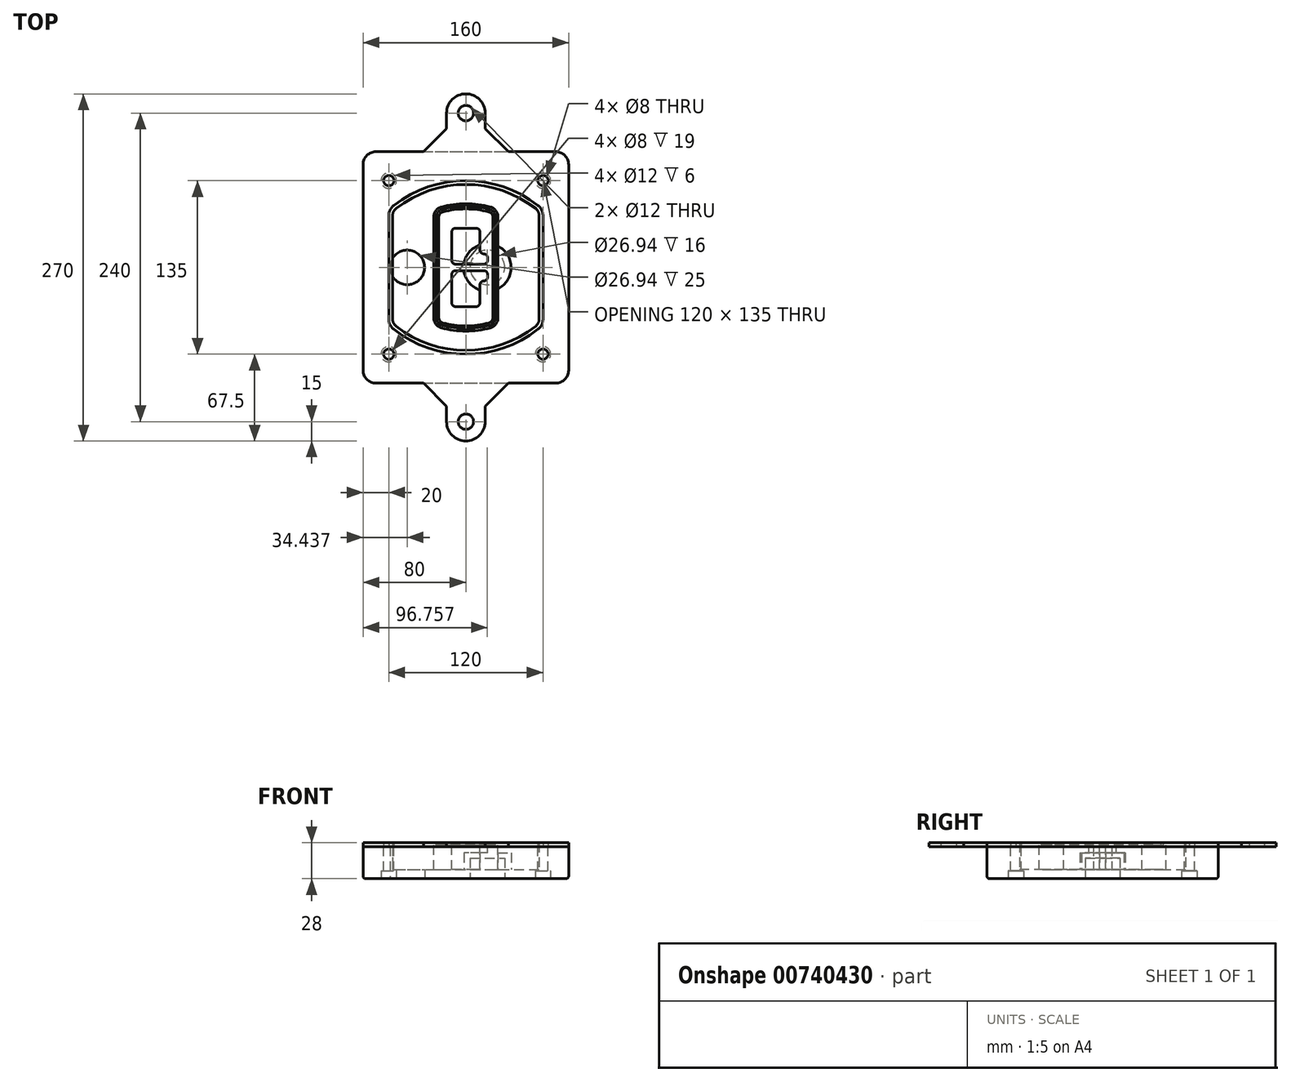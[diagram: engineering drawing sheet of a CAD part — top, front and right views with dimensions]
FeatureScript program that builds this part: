
annotation { "Feature Type Name" : "Feature", "Feature Type Description" : "" }
export const myFeature = defineFeature(function(context is Context, id is Id, definition is map)
    precondition{}
    {
        {
            var Q0;
            Q0=qCreatedBy(makeId("Top.planeOp"),FACE);
            var sketch = newSketch(context, id + "F0", { "sketchPlane" : qUnion([Q0])});
            skPoint(sketch, "E0.rect.middle", {"position": v(0, 0) * mm});
            skLineSegment(sketch, "E1.bottom", {"start": v(-70, -90) * mm, "end": v(70, -90) * mm});
            skLineSegment(sketch, "E1.top", {"start": v(-70, 90) * mm, "end": v(70, 90) * mm});
            skLineSegment(sketch, "E1.left", {"start": v(-80, -80) * mm, "end": v(-80, 80) * mm});
            skLineSegment(sketch, "E1.right", {"start": v(80, -80) * mm, "end": v(80, 80) * mm});
            skLineSegment(sketch, "E2", {"start": v(-80, 90) * mm, "end": v(80, -90) * mm, "construction": true});
            skLineSegment(sketch, "E3", {"start": v(80, 90) * mm, "end": v(-80, -90) * mm, "construction": true});
            skCircle(sketch, "E4", {"center": v(-60, 67.5) * mm, "radius": 4 * mm});
            skCircle(sketch, "E5", {"center": v(60, 67.5) * mm, "radius": 4 * mm});
            skCircle(sketch, "E6", {"center": v(60, -67.5) * mm, "radius": 4 * mm});
            skCircle(sketch, "E7", {"center": v(-60, -67.5) * mm, "radius": 4 * mm});
            skLineSegment(sketch, "E8", {"start": v(-60, 67.5) * mm, "end": v(60, 67.5) * mm, "construction": true});
            skLineSegment(sketch, "E9", {"start": v(60, 67.5) * mm, "end": v(60, -67.5) * mm, "construction": true});
            skLineSegment(sketch, "E10", {"start": v(60, -67.5) * mm, "end": v(-60, -67.5) * mm, "construction": true});
            skLineSegment(sketch, "E11", {"start": v(-60, -67.5) * mm, "end": v(-60, 67.5) * mm, "construction": true});
            skLineSegment(sketch, "E12", {"start": v(-60, 40.3) * mm, "end": v(-60, -40.3) * mm});
            skLineSegment(sketch, "E13", {"start": v(60, 40.3) * mm, "end": v(60, -40.3) * mm});
            skArc(sketch, "E14", {"start": v(56.15, 48.18) * mm, "mid": v(0, 67.5) * mm, "end": v(-56.15, 48.18) * mm});
            skArc(sketch, "E15", {"start": v(-56.15, -48.18) * mm, "mid": v(0, -67.5) * mm, "end": v(56.15, -48.18) * mm});
            skLineSegment(sketch, "E16", {"start": v(-60, 0) * mm, "end": v(60, 0) * mm, "construction": true});
            skPoint(sketch, "E17.visualSharp", {"position": v(-60, -45) * mm});
            skArc(sketch, "E17.filletArc", {"start": v(-60, -40.3) * mm, "mid": v(-58.99, -44.68) * mm, "end": v(-56.15, -48.18) * mm});
            skPoint(sketch, "E18.visualSharp", {"position": v(-60, 45) * mm});
            skArc(sketch, "E18.filletArc", {"start": v(-56.15, 48.18) * mm, "mid": v(-58.99, 44.68) * mm, "end": v(-60, 40.3) * mm});
            skPoint(sketch, "E19.visualSharp", {"position": v(60, 45) * mm});
            skArc(sketch, "E19.filletArc", {"start": v(60, 40.3) * mm, "mid": v(58.99, 44.68) * mm, "end": v(56.15, 48.18) * mm});
            skPoint(sketch, "E20.visualSharp", {"position": v(60, -45) * mm});
            skArc(sketch, "E20.filletArc", {"start": v(56.15, -48.18) * mm, "mid": v(58.99, -44.68) * mm, "end": v(60, -40.3) * mm});
            skPoint(sketch, "E21.visualSharp", {"position": v(-80, 90) * mm});
            skArc(sketch, "E21.filletArc", {"start": v(-70, 90) * mm, "mid": v(-77.07, 87.07) * mm, "end": v(-80, 80) * mm});
            skPoint(sketch, "E22.visualSharp", {"position": v(80, 90) * mm});
            skArc(sketch, "E22.filletArc", {"start": v(80, 80) * mm, "mid": v(77.07, 87.07) * mm, "end": v(70, 90) * mm});
            skPoint(sketch, "E23.visualSharp", {"position": v(80, -90) * mm});
            skArc(sketch, "E23.filletArc", {"start": v(70, -90) * mm, "mid": v(77.07, -87.07) * mm, "end": v(80, -80) * mm});
            skPoint(sketch, "E24.visualSharp", {"position": v(-80, -90) * mm});
            skArc(sketch, "E24.filletArc", {"start": v(-80, -80) * mm, "mid": v(-77.07, -87.07) * mm, "end": v(-70, -90) * mm});
            skArc(sketch, "E25.0", {"start": v(57, 40.3) * mm, "mid": v(56.3, 43.36) * mm, "end": v(54.3, 45.81) * mm});
            skLineSegment(sketch, "E25.1", {"start": v(57, 40.3) * mm, "end": v(57, -40.3) * mm});
            skArc(sketch, "E25.2", {"start": v(54.3, -45.81) * mm, "mid": v(56.3, -43.36) * mm, "end": v(57, -40.3) * mm});
            skArc(sketch, "E25.3", {"start": v(-54.3, -45.81) * mm, "mid": v(0, -64.5) * mm, "end": v(54.3, -45.81) * mm});
            skArc(sketch, "E25.4", {"start": v(-57, -40.3) * mm, "mid": v(-56.3, -43.36) * mm, "end": v(-54.3, -45.81) * mm});
            skArc(sketch, "E25.5", {"start": v(54.3, 45.81) * mm, "mid": v(0, 64.5) * mm, "end": v(-54.3, 45.81) * mm});
            skLineSegment(sketch, "E25.6", {"start": v(-57, 40.3) * mm, "end": v(-57, -40.3) * mm});
            skArc(sketch, "E25.7", {"start": v(-54.3, 45.81) * mm, "mid": v(-56.3, 43.36) * mm, "end": v(-57, 40.3) * mm});
            skArc(sketch, "E26.0", {"start": v(-58.62, 51.33) * mm, "mid": v(-62.58, 46.43) * mm, "end": v(-64, 40.3) * mm});
            skArc(sketch, "E26.1", {"start": v(58.62, 51.33) * mm, "mid": v(0, 71.5) * mm, "end": v(-58.62, 51.33) * mm});
            skArc(sketch, "E26.2", {"start": v(64, 40.3) * mm, "mid": v(62.58, 46.43) * mm, "end": v(58.62, 51.33) * mm});
            skLineSegment(sketch, "E26.3", {"start": v(64, 40.3) * mm, "end": v(64, -40.3) * mm});
            skArc(sketch, "E26.4", {"start": v(58.62, -51.33) * mm, "mid": v(62.58, -46.43) * mm, "end": v(64, -40.3) * mm});
            skLineSegment(sketch, "E26.5", {"start": v(-64, 40.3) * mm, "end": v(-64, -40.3) * mm});
            skArc(sketch, "E26.6", {"start": v(-58.62, -51.33) * mm, "mid": v(0, -71.5) * mm, "end": v(58.62, -51.33) * mm});
            skArc(sketch, "E26.7", {"start": v(-64, -40.3) * mm, "mid": v(-62.58, -46.43) * mm, "end": v(-58.62, -51.33) * mm});
            skSolve(sketch);
        }
        {
            var Q0;
            Q0=makeQuery(id+"F0.imprint","IMPRINT",FACE,{"disambiguationData":[TD([[makeQuery(id+"F0.imprint","IMPRINT",EDGE,{"derivedFrom":sQuery(id+"F0.wireOp",EDGE,"E1.bottom")}),1.0]])]});
            var Q1;
            Q1=makeQuery(id+"F0.imprint","IMPRINT",FACE,{"disambiguationData":[TD([[makeQuery(id+"F0.imprint","IMPRINT",EDGE,{"derivedFrom":sQuery(id+"F0.wireOp",EDGE,"E12")}),1.0]])]});
            var Q2;
            Q2=makeQuery(id+"F0.imprint","IMPRINT",FACE,{"disambiguationData":[TD([[makeQuery(id+"F0.imprint","IMPRINT",EDGE,{"derivedFrom":sQuery(id+"F0.wireOp",EDGE,"E25.0")}),1.0]])]});
            var Q3;
            Q3=makeQuery(id+"F0.imprint","IMPRINT",FACE,{"disambiguationData":[TD([[makeQuery(id+"F0.imprint","IMPRINT",EDGE,{"derivedFrom":sQuery(id+"F0.wireOp",EDGE,"E12")}),-1.0]])]});
            extrude(context, id + "F1", {"entities" : qUnion([Q0, Q1, Q2, Q3]), "oppositeDirection" : true, "depth" : 25 * mm});
        }
        {
            var Q0;
            Q0=makeQuery(id+"F0.imprint","IMPRINT",FACE,{"disambiguationData":[TD([[makeQuery(id+"F0.imprint","IMPRINT",EDGE,{"derivedFrom":sQuery(id+"F0.wireOp",EDGE,"E12")}),1.0]])]});
            extrude(context, id + "F2", {"entities" : qUnion([Q0]), "operationType" : NewBodyOperationType.ADD, "depth" : 3 * mm});
        }
        {
            var Q0;
            Q0=makeQuery(id+"F0.imprint","IMPRINT",FACE,{"disambiguationData":[TD([[makeQuery(id+"F0.imprint","IMPRINT",EDGE,{"derivedFrom":sQuery(id+"F0.wireOp",EDGE,"E25.0")}),1.0]])]});
            extrude(context, id + "F3", {"entities" : qUnion([Q0]), "operationType" : NewBodyOperationType.REMOVE, "oppositeDirection" : true, "depth" : 18 * mm});
        }
        {
            var Q0;
            Q0=makeQuery(id+"F2.opExtrude","CAP_FACE",FACE,{"disambiguationData":[OSD([sQuery(id+"F0.wireOp",EDGE,"E12"),sQuery(id+"F0.wireOp",EDGE,"E13"),sQuery(id+"F0.wireOp",EDGE,"E14"),sQuery(id+"F0.wireOp",EDGE,"E15"),sQuery(id+"F0.wireOp",EDGE,"E17.filletArc"),sQuery(id+"F0.wireOp",EDGE,"E18.filletArc"),sQuery(id+"F0.wireOp",EDGE,"E19.filletArc"),sQuery(id+"F0.wireOp",EDGE,"E20.filletArc"),sQuery(id+"F0.wireOp",EDGE,"E25.0"),sQuery(id+"F0.wireOp",EDGE,"E25.1"),sQuery(id+"F0.wireOp",EDGE,"E25.2"),sQuery(id+"F0.wireOp",EDGE,"E25.3"),sQuery(id+"F0.wireOp",EDGE,"E25.4"),sQuery(id+"F0.wireOp",EDGE,"E25.5"),sQuery(id+"F0.wireOp",EDGE,"E25.6"),sQuery(id+"F0.wireOp",EDGE,"E25.7")])],"isStart":false});
            var sketch = newSketch(context, id + "F4", { "sketchPlane" : qUnion([Q0])});
            skArc(sketch, "E27.0", {"start": v(-19.08, -46.97) * mm, "mid": v(0, -49.5) * mm, "end": v(19.08, -46.97) * mm});
            skArc(sketch, "E28.0", {"start": v(19.08, 46.97) * mm, "mid": v(0, 49.5) * mm, "end": v(-19.08, 46.97) * mm});
            skLineSegment(sketch, "E29", {"start": v(-25, 39.25) * mm, "end": v(-25, -39.25) * mm});
            skLineSegment(sketch, "E30", {"start": v(25, 39.25) * mm, "end": v(25, -39.25) * mm});
            skLineSegment(sketch, "E31", {"start": v(-25, 45.1) * mm, "end": v(25, 45.1) * mm, "construction": true});
            skLineSegment(sketch, "E32", {"start": v(-25, -45.1) * mm, "end": v(25, -45.1) * mm, "construction": true});
            skPoint(sketch, "E33.visualSharp", {"position": v(-25, 45.1) * mm});
            skArc(sketch, "E33.filletArc", {"start": v(-19.08, 46.97) * mm, "mid": v(-23.35, 44.11) * mm, "end": v(-25, 39.25) * mm});
            skPoint(sketch, "E34.visualSharp", {"position": v(25, 45.1) * mm});
            skArc(sketch, "E34.filletArc", {"start": v(25, 39.25) * mm, "mid": v(23.35, 44.11) * mm, "end": v(19.08, 46.97) * mm});
            skPoint(sketch, "E35.visualSharp", {"position": v(25, -45.1) * mm});
            skArc(sketch, "E35.filletArc", {"start": v(19.08, -46.97) * mm, "mid": v(23.35, -44.11) * mm, "end": v(25, -39.25) * mm});
            skPoint(sketch, "E36.visualSharp", {"position": v(-25, -45.1) * mm});
            skArc(sketch, "E36.filletArc", {"start": v(-25, -39.25) * mm, "mid": v(-23.35, -44.11) * mm, "end": v(-19.08, -46.97) * mm});
            skArc(sketch, "E37.0", {"start": v(54.3, 45.81) * mm, "mid": v(0, 64.5) * mm, "end": v(-54.3, 45.81) * mm});
            skArc(sketch, "E37.1", {"start": v(-54.3, 45.81) * mm, "mid": v(-56.3, 43.36) * mm, "end": v(-57, 40.3) * mm});
            skLineSegment(sketch, "E37.2", {"start": v(-57, 40.3) * mm, "end": v(-57, -40.3) * mm});
            skArc(sketch, "E37.3", {"start": v(-57, -40.3) * mm, "mid": v(-56.3, -43.36) * mm, "end": v(-54.3, -45.81) * mm});
            skArc(sketch, "E37.4", {"start": v(-54.3, -45.81) * mm, "mid": v(0, -64.5) * mm, "end": v(54.3, -45.81) * mm});
            skArc(sketch, "E37.5", {"start": v(54.3, -45.81) * mm, "mid": v(56.3, -43.36) * mm, "end": v(57, -40.3) * mm});
            skLineSegment(sketch, "E37.6", {"start": v(57, 40.3) * mm, "end": v(57, -40.3) * mm});
            skArc(sketch, "E37.7", {"start": v(57, 40.3) * mm, "mid": v(56.3, 43.36) * mm, "end": v(54.3, 45.81) * mm});
            skLineSegment(sketch, "E38.0", {"start": v(23, 39.25) * mm, "end": v(23, -39.25) * mm});
            skArc(sketch, "E38.1", {"start": v(18.56, -45.04) * mm, "mid": v(21.76, -42.9) * mm, "end": v(23, -39.25) * mm});
            skArc(sketch, "E38.2", {"start": v(-18.56, -45.04) * mm, "mid": v(0, -47.5) * mm, "end": v(18.56, -45.04) * mm});
            skArc(sketch, "E38.3", {"start": v(-23, -39.25) * mm, "mid": v(-21.76, -42.9) * mm, "end": v(-18.56, -45.04) * mm});
            skLineSegment(sketch, "E38.4", {"start": v(-23, 39.25) * mm, "end": v(-23, -39.25) * mm});
            skArc(sketch, "E38.5", {"start": v(23, 39.25) * mm, "mid": v(21.76, 42.9) * mm, "end": v(18.56, 45.04) * mm});
            skArc(sketch, "E38.6", {"start": v(-18.56, 45.04) * mm, "mid": v(-21.76, 42.9) * mm, "end": v(-23, 39.25) * mm});
            skArc(sketch, "E38.7", {"start": v(18.56, 45.04) * mm, "mid": v(0, 47.5) * mm, "end": v(-18.56, 45.04) * mm});
            skArc(sketch, "E39.0", {"start": v(21, 39.25) * mm, "mid": v(20.18, 41.68) * mm, "end": v(18.04, 43.1) * mm});
            skLineSegment(sketch, "E39.1", {"start": v(21, 39.25) * mm, "end": v(21, -39.25) * mm});
            skArc(sketch, "E39.2", {"start": v(18.04, -43.1) * mm, "mid": v(20.18, -41.68) * mm, "end": v(21, -39.25) * mm});
            skArc(sketch, "E39.3", {"start": v(-18.04, -43.1) * mm, "mid": v(0, -45.5) * mm, "end": v(18.04, -43.1) * mm});
            skArc(sketch, "E39.4", {"start": v(-21, -39.25) * mm, "mid": v(-20.18, -41.68) * mm, "end": v(-18.04, -43.1) * mm});
            skArc(sketch, "E39.5", {"start": v(18.04, 43.1) * mm, "mid": v(0, 45.5) * mm, "end": v(-18.04, 43.1) * mm});
            skLineSegment(sketch, "E39.6", {"start": v(-21, 39.25) * mm, "end": v(-21, -39.25) * mm});
            skArc(sketch, "E39.7", {"start": v(-18.04, 43.1) * mm, "mid": v(-20.18, 41.68) * mm, "end": v(-21, 39.25) * mm});
            skLineSegment(sketch, "E40", {"start": v(-25, 0) * mm, "end": v(25, 0) * mm, "construction": true});
            skLineSegment(sketch, "E41", {"start": v(-11, 5.5) * mm, "end": v(-11, 27.5) * mm});
            skLineSegment(sketch, "E42", {"start": v(-8, 30.5) * mm, "end": v(8, 30.5) * mm});
            skLineSegment(sketch, "E43", {"start": v(11, 27.5) * mm, "end": v(11, 13.5) * mm});
            skLineSegment(sketch, "E44", {"start": v(14, 10.5) * mm, "end": v(14, 10.5) * mm});
            skLineSegment(sketch, "E45", {"start": v(17, 7.5) * mm, "end": v(17, 5.5) * mm});
            skLineSegment(sketch, "E46", {"start": v(14, 2.5) * mm, "end": v(-8, 2.5) * mm});
            skPoint(sketch, "E47.visualSharp", {"position": v(-11, 30.5) * mm});
            skArc(sketch, "E47.filletArc", {"start": v(-8, 30.5) * mm, "mid": v(-10.12, 29.62) * mm, "end": v(-11, 27.5) * mm});
            skPoint(sketch, "E48.visualSharp", {"position": v(11, 30.5) * mm});
            skArc(sketch, "E48.filletArc", {"start": v(11, 27.5) * mm, "mid": v(10.12, 29.62) * mm, "end": v(8, 30.5) * mm});
            skPoint(sketch, "E49.visualSharp", {"position": v(11, 10.5) * mm});
            skArc(sketch, "E49.filletArc", {"start": v(11, 13.5) * mm, "mid": v(11.88, 11.38) * mm, "end": v(14, 10.5) * mm});
            skPoint(sketch, "E50.visualSharp", {"position": v(17, 10.5) * mm});
            skArc(sketch, "E50.filletArc", {"start": v(17, 7.5) * mm, "mid": v(16.12, 9.62) * mm, "end": v(14, 10.5) * mm});
            skPoint(sketch, "E51.visualSharp", {"position": v(17, 2.5) * mm});
            skArc(sketch, "E51.filletArc", {"start": v(14, 2.5) * mm, "mid": v(16.12, 3.38) * mm, "end": v(17, 5.5) * mm});
            skPoint(sketch, "E52.visualSharp", {"position": v(-11, 2.5) * mm});
            skArc(sketch, "E52.filletArc", {"start": v(-11, 5.5) * mm, "mid": v(-10.12, 3.38) * mm, "end": v(-8, 2.5) * mm});
            skLineSegment(sketch, "E53.0.MirrorCS", {"start": v(14, -2.5) * mm, "end": v(-8, -2.5) * mm});
            skArc(sketch, "E54.0.MirrorCS", {"start": v(-11, -5.5) * mm, "mid": v(-10.12, -3.38) * mm, "end": v(-8, -2.5) * mm});
            skLineSegment(sketch, "E55.0.MirrorCS", {"start": v(-11, -5.5) * mm, "end": v(-11, -27.5) * mm});
            skArc(sketch, "E56.0.MirrorCS", {"start": v(-8, -30.5) * mm, "mid": v(-10.12, -29.62) * mm, "end": v(-11, -27.5) * mm});
            skLineSegment(sketch, "E57.0.MirrorCS", {"start": v(-8, -30.5) * mm, "end": v(8, -30.5) * mm});
            skArc(sketch, "E58.0.MirrorCS", {"start": v(11, -27.5) * mm, "mid": v(10.12, -29.62) * mm, "end": v(8, -30.5) * mm});
            skLineSegment(sketch, "E59.0.MirrorCS", {"start": v(11, -27.5) * mm, "end": v(11, -13.5) * mm});
            skArc(sketch, "E60.0.MirrorCS", {"start": v(11, -13.5) * mm, "mid": v(11.88, -11.38) * mm, "end": v(14, -10.5) * mm});
            skArc(sketch, "E61.0.MirrorCS", {"start": v(17, -7.5) * mm, "mid": v(16.12, -9.62) * mm, "end": v(14, -10.5) * mm});
            skLineSegment(sketch, "E62.0.MirrorCS", {"start": v(17, -7.5) * mm, "end": v(17, -5.5) * mm});
            skArc(sketch, "E63.0.MirrorCS", {"start": v(14, -2.5) * mm, "mid": v(16.12, -3.38) * mm, "end": v(17, -5.5) * mm});
            skSolve(sketch);
        }
        {
            var Q0;
            Q0=makeQuery(id+"F4.imprint","IMPRINT",FACE,{"disambiguationData":[TD([[makeQuery(id+"F4.imprint","IMPRINT",EDGE,{"derivedFrom":sQuery(id+"F4.wireOp",EDGE,"E27.0")}),1.0]])]});
            var Q1;
            Q1=makeQuery(id+"F4.imprint","IMPRINT",FACE,{"disambiguationData":[TD([[makeQuery(id+"F4.imprint","IMPRINT",EDGE,{"derivedFrom":sQuery(id+"F4.wireOp",EDGE,"E38.0")}),-1.0]])]});
            var Q2;
            Q2=makeQuery(id+"F4.imprint","IMPRINT",FACE,{"disambiguationData":[TD([[makeQuery(id+"F4.imprint","IMPRINT",EDGE,{"derivedFrom":sQuery(id+"F4.wireOp",EDGE,"E39.0")}),1.0]])]});
            extrude(context, id + "F5", {"entities" : qUnion([Q0, Q1, Q2]), "operationType" : NewBodyOperationType.ADD, "endBound" : BoundingType.UP_TO_NEXT, "oppositeDirection" : true, "depth" : 25 * mm});
        }
        {
            var Q0;
            Q0=makeQuery(id+"F4.imprint","IMPRINT",FACE,{"disambiguationData":[TD([[makeQuery(id+"F4.imprint","IMPRINT",EDGE,{"derivedFrom":sQuery(id+"F4.wireOp",EDGE,"E38.0")}),-1.0]])]});
            extrude(context, id + "F6", {"entities" : qUnion([Q0]), "operationType" : NewBodyOperationType.REMOVE, "oppositeDirection" : true, "depth" : 2 * mm});
        }
        {
            var Q0;
            Q0=makeQuery(id+"F1.opExtrude","CAP_FACE",FACE,{"disambiguationData":[OSD([sQuery(id+"F0.wireOp",EDGE,"E1.bottom"),sQuery(id+"F0.wireOp",EDGE,"E1.top"),sQuery(id+"F0.wireOp",EDGE,"E1.left"),sQuery(id+"F0.wireOp",EDGE,"E1.right"),sQuery(id+"F0.wireOp",EDGE,"E4"),sQuery(id+"F0.wireOp",EDGE,"E5"),sQuery(id+"F0.wireOp",EDGE,"E6"),sQuery(id+"F0.wireOp",EDGE,"E7"),sQuery(id+"F0.wireOp",EDGE,"E21.filletArc"),sQuery(id+"F0.wireOp",EDGE,"E22.filletArc"),sQuery(id+"F0.wireOp",EDGE,"E23.filletArc"),sQuery(id+"F0.wireOp",EDGE,"E24.filletArc")])],"isStart":false});
            var sketch = newSketch(context, id + "F7", { "sketchPlane" : qUnion([Q0])});
            skCircle(sketch, "E64", {"center": v(16.76, 0) * mm, "radius": 13.47 * mm});
            skCircle(sketch, "E65", {"center": v(-45.56, 0) * mm, "radius": 13.47 * mm});
            skLineSegment(sketch, "E66", {"start": v(80, 0) * mm, "end": v(-80, 0) * mm});
            skCircle(sketch, "E67", {"center": v(16.76, 0) * mm, "radius": 18.47 * mm});
            skCircle(sketch, "E68", {"center": v(60, -67.5) * mm, "radius": 6 * mm});
            skCircle(sketch, "E69", {"center": v(-60, -67.5) * mm, "radius": 6 * mm});
            skCircle(sketch, "E70", {"center": v(-60, 67.5) * mm, "radius": 6 * mm});
            skCircle(sketch, "E71", {"center": v(60, 67.5) * mm, "radius": 6 * mm});
            skSolve(sketch);
        }
        {
            var Q0;
            {var subQ1=sQuery(id+"F7.wireOp",EDGE,"E66");var subQ4=sQuery(id+"F7.wireOp",EDGE,"E64");var subQ6=makeQuery(id+"F7.imprint","INTERSECT",VERTEX,{"disambiguationData":[OD(0.0)],"derivedFrom":[subQ4,subQ1]});Q0=makeQuery(id+"F7.imprint","IMPRINT",FACE,{"disambiguationData":[TD([[makeQuery(id+"F7.imprint","IMPRINT",EDGE,{"disambiguationData":[TD([[subQ6,-1.0]])],"derivedFrom":subQ4}),-1.0]])]});}
            var Q1;
            {var subQ0=sQuery(id+"F7.wireOp",EDGE,"E66");var subQ1=sQuery(id+"F7.wireOp",EDGE,"E64");var subQ3=makeQuery(id+"F7.imprint","INTERSECT",VERTEX,{"disambiguationData":[OD(0.0)],"derivedFrom":[subQ1,subQ0]});Q1=makeQuery(id+"F7.imprint","IMPRINT",FACE,{"disambiguationData":[TD([[makeQuery(id+"F7.imprint","IMPRINT",EDGE,{"disambiguationData":[TD([[subQ3,-1.0]])],"derivedFrom":subQ1}),1.0]])]});}
            var Q2;
            {var subQ0=sQuery(id+"F7.wireOp",EDGE,"E66");var subQ1=sQuery(id+"F7.wireOp",EDGE,"E64");var subQ3=makeQuery(id+"F7.imprint","INTERSECT",VERTEX,{"disambiguationData":[OD(0.0)],"derivedFrom":[subQ1,subQ0]});Q2=makeQuery(id+"F7.imprint","IMPRINT",FACE,{"disambiguationData":[TD([[makeQuery(id+"F7.imprint","IMPRINT",EDGE,{"disambiguationData":[TD([[subQ3,1.0]])],"derivedFrom":subQ1}),1.0]])]});}
            var Q3;
            {var subQ1=sQuery(id+"F7.wireOp",EDGE,"E66");var subQ4=sQuery(id+"F7.wireOp",EDGE,"E64");var subQ6=makeQuery(id+"F7.imprint","INTERSECT",VERTEX,{"disambiguationData":[OD(0.0)],"derivedFrom":[subQ4,subQ1]});Q3=makeQuery(id+"F7.imprint","IMPRINT",FACE,{"disambiguationData":[TD([[makeQuery(id+"F7.imprint","IMPRINT",EDGE,{"disambiguationData":[TD([[subQ6,1.0]])],"derivedFrom":subQ4}),-1.0]])]});}
            extrude(context, id + "F8", {"entities" : qUnion([Q0, Q1, Q2, Q3]), "operationType" : NewBodyOperationType.ADD, "oppositeDirection" : true, "depth" : 20 * mm});
        }
        {
            var Q0;
            {var subQ0=sQuery(id+"F7.wireOp",EDGE,"E66");var subQ1=sQuery(id+"F7.wireOp",EDGE,"E64");var subQ3=makeQuery(id+"F7.imprint","INTERSECT",VERTEX,{"disambiguationData":[OD(0.0)],"derivedFrom":[subQ1,subQ0]});Q0=makeQuery(id+"F7.imprint","IMPRINT",FACE,{"disambiguationData":[TD([[makeQuery(id+"F7.imprint","IMPRINT",EDGE,{"disambiguationData":[TD([[subQ3,-1.0]])],"derivedFrom":subQ1}),1.0]])]});}
            var Q1;
            {var subQ0=sQuery(id+"F7.wireOp",EDGE,"E66");var subQ1=sQuery(id+"F7.wireOp",EDGE,"E64");var subQ3=makeQuery(id+"F7.imprint","INTERSECT",VERTEX,{"disambiguationData":[OD(0.0)],"derivedFrom":[subQ1,subQ0]});Q1=makeQuery(id+"F7.imprint","IMPRINT",FACE,{"disambiguationData":[TD([[makeQuery(id+"F7.imprint","IMPRINT",EDGE,{"disambiguationData":[TD([[subQ3,1.0]])],"derivedFrom":subQ1}),1.0]])]});}
            extrude(context, id + "F9", {"entities" : qUnion([Q0, Q1]), "operationType" : NewBodyOperationType.REMOVE, "oppositeDirection" : true, "depth" : 16 * mm});
        }
        {
            var Q0;
            {var subQ0=sQuery(id+"F7.wireOp",EDGE,"E66");var subQ1=sQuery(id+"F7.wireOp",EDGE,"E65");var subQ3=makeQuery(id+"F7.imprint","INTERSECT",VERTEX,{"disambiguationData":[OD(0.0)],"derivedFrom":[subQ1,subQ0]});Q0=makeQuery(id+"F7.imprint","IMPRINT",FACE,{"disambiguationData":[TD([[makeQuery(id+"F7.imprint","IMPRINT",EDGE,{"disambiguationData":[TD([[subQ3,-1.0]])],"derivedFrom":subQ1}),1.0]])]});}
            var Q1;
            {var subQ0=sQuery(id+"F7.wireOp",EDGE,"E66");var subQ1=sQuery(id+"F7.wireOp",EDGE,"E65");var subQ3=makeQuery(id+"F7.imprint","INTERSECT",VERTEX,{"disambiguationData":[OD(0.0)],"derivedFrom":[subQ1,subQ0]});Q1=makeQuery(id+"F7.imprint","IMPRINT",FACE,{"disambiguationData":[TD([[makeQuery(id+"F7.imprint","IMPRINT",EDGE,{"disambiguationData":[TD([[subQ3,1.0]])],"derivedFrom":subQ1}),1.0]])]});}
            extrude(context, id + "F10", {"entities" : qUnion([Q0, Q1]), "operationType" : NewBodyOperationType.REMOVE, "oppositeDirection" : true, "depth" : 25 * mm});
        }
        {
            var Q0;
            Q0=makeQuery(id+"F7.imprint","IMPRINT",FACE,{"disambiguationData":[TD([[makeQuery(id+"F7.imprint","IMPRINT",EDGE,{"derivedFrom":sQuery(id+"F7.wireOp",EDGE,"E68")}),1.0]])]});
            var Q1;
            Q1=makeQuery(id+"F7.imprint","IMPRINT",FACE,{"disambiguationData":[TD([[makeQuery(id+"F7.imprint","IMPRINT",EDGE,{"derivedFrom":makeQuery(id+"F1.opExtrude","CAP_EDGE",EDGE,{"disambiguationData":[OSD([sQuery(id+"F0.wireOp",EDGE,"E5")])],"isStart":false})}),-1.0]])]});
            var Q2;
            Q2=makeQuery(id+"F7.imprint","IMPRINT",FACE,{"disambiguationData":[TD([[makeQuery(id+"F7.imprint","IMPRINT",EDGE,{"derivedFrom":sQuery(id+"F7.wireOp",EDGE,"E69")}),1.0]])]});
            var Q3;
            Q3=makeQuery(id+"F7.imprint","IMPRINT",FACE,{"disambiguationData":[TD([[makeQuery(id+"F7.imprint","IMPRINT",EDGE,{"derivedFrom":makeQuery(id+"F1.opExtrude","CAP_EDGE",EDGE,{"disambiguationData":[OSD([sQuery(id+"F0.wireOp",EDGE,"E4")])],"isStart":false})}),-1.0]])]});
            var Q4;
            Q4=makeQuery(id+"F7.imprint","IMPRINT",FACE,{"disambiguationData":[TD([[makeQuery(id+"F7.imprint","IMPRINT",EDGE,{"derivedFrom":sQuery(id+"F7.wireOp",EDGE,"E70")}),1.0]])]});
            var Q5;
            Q5=makeQuery(id+"F7.imprint","IMPRINT",FACE,{"disambiguationData":[TD([[makeQuery(id+"F7.imprint","IMPRINT",EDGE,{"derivedFrom":makeQuery(id+"F1.opExtrude","CAP_EDGE",EDGE,{"disambiguationData":[OSD([sQuery(id+"F0.wireOp",EDGE,"E7")])],"isStart":false})}),-1.0]])]});
            var Q6;
            Q6=makeQuery(id+"F7.imprint","IMPRINT",FACE,{"disambiguationData":[TD([[makeQuery(id+"F7.imprint","IMPRINT",EDGE,{"derivedFrom":sQuery(id+"F7.wireOp",EDGE,"E71")}),1.0]])]});
            var Q7;
            Q7=makeQuery(id+"F7.imprint","IMPRINT",FACE,{"disambiguationData":[TD([[makeQuery(id+"F7.imprint","IMPRINT",EDGE,{"derivedFrom":makeQuery(id+"F1.opExtrude","CAP_EDGE",EDGE,{"disambiguationData":[OSD([sQuery(id+"F0.wireOp",EDGE,"E6")])],"isStart":false})}),-1.0]])]});
            extrude(context, id + "F11", {"entities" : qUnion([Q0, Q1, Q2, Q3, Q4, Q5, Q6, Q7]), "operationType" : NewBodyOperationType.REMOVE, "oppositeDirection" : true, "depth" : 6 * mm});
        }
        {
            var Q0;
            Q0=makeQuery(id+"F1.opExtrude","CAP_EDGE",EDGE,{"disambiguationData":[OSD([sQuery(id+"F0.wireOp",EDGE,"E1.bottom")])],"isStart":false});
            fillet(context, id + "F12", {"entities" : qUnion([Q0]), "radius" : 2 * mm, "tangentPropagation" : true, "allowEdgeOverflow" : false});
        }
        {
            var Q0;
            Q0=qCreatedBy(makeId("Top.planeOp"),FACE);
            var sketch = newSketch(context, id + "F13", { "sketchPlane" : qUnion([Q0])});
            skLineSegment(sketch, "E72.0", {"start": v(-70, 90) * mm, "end": v(70, 90) * mm});
            skArc(sketch, "E72.1", {"start": v(-70, 90) * mm, "mid": v(-77.07, 87.07) * mm, "end": v(-80, 80) * mm});
            skLineSegment(sketch, "E72.2", {"start": v(-80, -80) * mm, "end": v(-80, 80) * mm});
            skArc(sketch, "E72.3", {"start": v(56.15, 48.18) * mm, "mid": v(0, 67.5) * mm, "end": v(-56.15, 48.18) * mm});
            skArc(sketch, "E72.4", {"start": v(-56.15, 48.18) * mm, "mid": v(-58.99, 44.68) * mm, "end": v(-60, 40.3) * mm});
            skLineSegment(sketch, "E72.5", {"start": v(-60, 40.3) * mm, "end": v(-60, -40.3) * mm});
            skArc(sketch, "E72.6", {"start": v(-60, -40.3) * mm, "mid": v(-58.99, -44.68) * mm, "end": v(-56.15, -48.18) * mm});
            skArc(sketch, "E72.7", {"start": v(-56.15, -48.18) * mm, "mid": v(0, -67.5) * mm, "end": v(56.15, -48.18) * mm});
            skLineSegment(sketch, "E72.8", {"start": v(60, 40.3) * mm, "end": v(60, -40.3) * mm});
            skArc(sketch, "E72.9", {"start": v(60, 40.3) * mm, "mid": v(58.99, 44.68) * mm, "end": v(56.15, 48.18) * mm});
            skArc(sketch, "E72.10", {"start": v(56.15, -48.18) * mm, "mid": v(58.99, -44.68) * mm, "end": v(60, -40.3) * mm});
            skLineSegment(sketch, "E72.11", {"start": v(80, -80) * mm, "end": v(80, 80) * mm});
            skArc(sketch, "E72.12", {"start": v(80, 80) * mm, "mid": v(77.07, 87.07) * mm, "end": v(70, 90) * mm});
            skLineSegment(sketch, "E72.13", {"start": v(-70, -90) * mm, "end": v(70, -90) * mm});
            skArc(sketch, "E72.14", {"start": v(70, -90) * mm, "mid": v(77.07, -87.07) * mm, "end": v(80, -80) * mm});
            skArc(sketch, "E72.15", {"start": v(-80, -80) * mm, "mid": v(-77.07, -87.07) * mm, "end": v(-70, -90) * mm});
            skCircle(sketch, "E72.16", {"center": v(-60, 67.5) * mm, "radius": 4 * mm});
            skCircle(sketch, "E72.17", {"center": v(60, 67.5) * mm, "radius": 4 * mm});
            skCircle(sketch, "E72.18", {"center": v(60, -67.5) * mm, "radius": 4 * mm});
            skCircle(sketch, "E72.19", {"center": v(-60, -67.5) * mm, "radius": 4 * mm});
            skLineSegment(sketch, "E73", {"start": v(0, 90) * mm, "end": v(0, 120) * mm, "construction": true});
            skPoint(sketch, "E73.endSnap0", {"position": v(0, 90) * mm});
            skArc(sketch, "E74", {"start": v(15, 120) * mm, "mid": v(0, 135) * mm, "end": v(-15, 120) * mm});
            skLineSegment(sketch, "E75", {"start": v(-15, 120) * mm, "end": v(-15, 108) * mm});
            skLineSegment(sketch, "E76", {"start": v(15, 120) * mm, "end": v(15, 108) * mm});
            skLineSegment(sketch, "E77", {"start": v(15, 108) * mm, "end": v(33, 90) * mm});
            skLineSegment(sketch, "E78", {"start": v(-15, 108) * mm, "end": v(-33, 90) * mm});
            skCircle(sketch, "E79", {"center": v(0, 120) * mm, "radius": 6 * mm});
            skLineSegment(sketch, "E80", {"start": v(-80, 0) * mm, "end": v(80, 0) * mm, "construction": true});
            skLineSegment(sketch, "E81.MirrorCS", {"start": v(-15, -108) * mm, "end": v(-33, -90) * mm});
            skLineSegment(sketch, "E82.MirrorCS", {"start": v(-15, -120) * mm, "end": v(-15, -108) * mm});
            skArc(sketch, "E83.MirrorCS", {"start": v(15, -120) * mm, "mid": v(0, -135) * mm, "end": v(-15, -120) * mm});
            skCircle(sketch, "E84.MirrorC", {"center": v(0, -120) * mm, "radius": 6 * mm});
            skLineSegment(sketch, "E85.MirrorCS", {"start": v(15, -120) * mm, "end": v(15, -108) * mm});
            skLineSegment(sketch, "E86.MirrorCS", {"start": v(15, -108) * mm, "end": v(33, -90) * mm});
            skLineSegment(sketch, "E87.MirrorCS", {"start": v(0, -90) * mm, "end": v(0, -120) * mm, "construction": true});
            skSolve(sketch);
        }
        {
            var Q0;
            Q0=qSketchRegion(id+"F13",true);
            var Q1;
            Q1=makeQuery(id+"F2.opExtrude","CAP_FACE",FACE,{"disambiguationData":[OSD([sQuery(id+"F0.wireOp",EDGE,"E12"),sQuery(id+"F0.wireOp",EDGE,"E13"),sQuery(id+"F0.wireOp",EDGE,"E14"),sQuery(id+"F0.wireOp",EDGE,"E15"),sQuery(id+"F0.wireOp",EDGE,"E17.filletArc"),sQuery(id+"F0.wireOp",EDGE,"E18.filletArc"),sQuery(id+"F0.wireOp",EDGE,"E19.filletArc"),sQuery(id+"F0.wireOp",EDGE,"E20.filletArc"),sQuery(id+"F0.wireOp",EDGE,"E25.0"),sQuery(id+"F0.wireOp",EDGE,"E25.1"),sQuery(id+"F0.wireOp",EDGE,"E25.2"),sQuery(id+"F0.wireOp",EDGE,"E25.3"),sQuery(id+"F0.wireOp",EDGE,"E25.4"),sQuery(id+"F0.wireOp",EDGE,"E25.5"),sQuery(id+"F0.wireOp",EDGE,"E25.6"),sQuery(id+"F0.wireOp",EDGE,"E25.7")])],"isStart":false});
            extrude(context, id + "F14", {"entities" : qUnion([Q0]), "endBound" : BoundingType.UP_TO_SURFACE, "endBoundEntityFace" : qUnion([Q1]), "depth" : 25 * mm});
        }
    });
